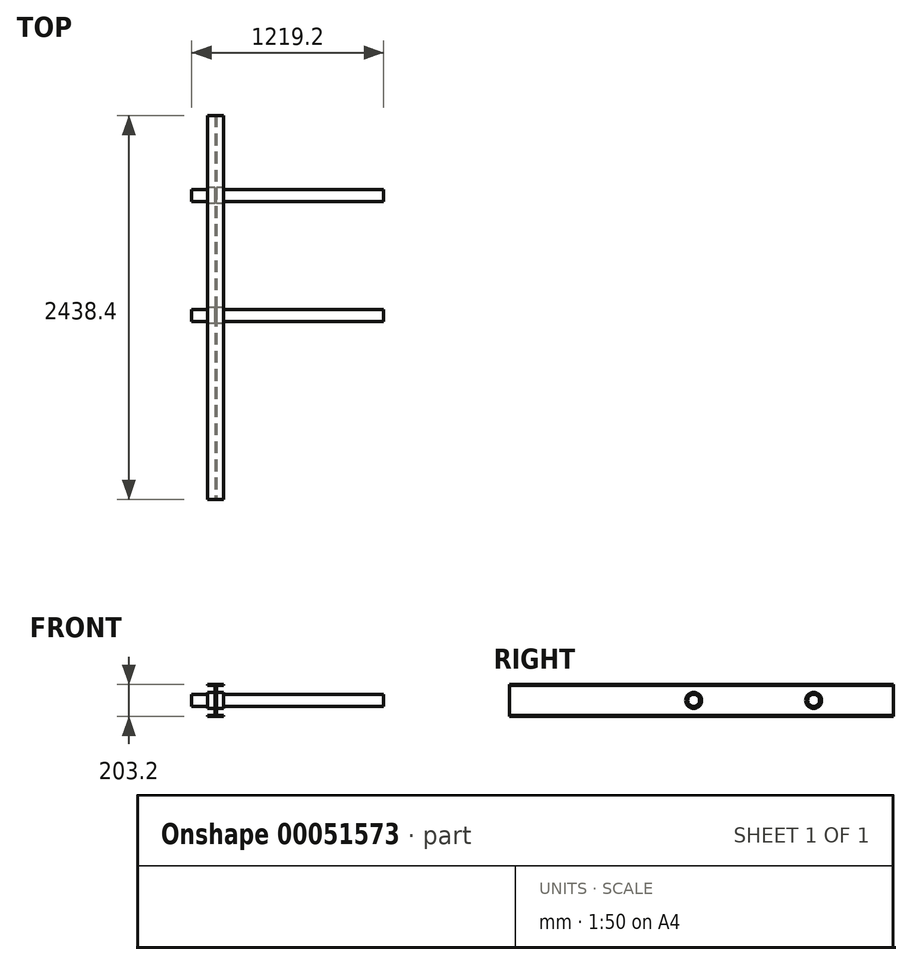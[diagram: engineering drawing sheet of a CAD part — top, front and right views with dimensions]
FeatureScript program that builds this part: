
annotation { "Feature Type Name" : "Feature", "Feature Type Description" : "" }
export const myFeature = defineFeature(function(context is Context, id is Id, definition is map)
    precondition{}
    {
        {
            var Q0;
            Q0=qCreatedBy(makeId("Front.planeOp"),FACE);
            var sketch = newSketch(context, id + "F0", { "sketchPlane" : qUnion([Q0])});
            skLineSegment(sketch, "E0.rect.bottom", {"start": v(50.8, -101.6) * mm, "end": v(-50.8, -101.6) * mm});
            skLineSegment(sketch, "E0.rect.top", {"start": v(50.8, 101.6) * mm, "end": v(-50.8, 101.6) * mm});
            skLineSegment(sketch, "E0.rect.left", {"start": v(50.8, -101.6) * mm, "end": v(50.8, 101.6) * mm});
            skLineSegment(sketch, "E0.rect.right", {"start": v(-50.8, -101.6) * mm, "end": v(-50.8, 101.6) * mm});
            skPoint(sketch, "E0.rect.middle", {"position": v(0, 0) * mm});
            skLineSegment(sketch, "E1.bottom", {"start": v(-50.8, 95.25) * mm, "end": v(-4.76, 95.25) * mm});
            skLineSegment(sketch, "E1.top", {"start": v(-50.8, -95.25) * mm, "end": v(-4.76, -95.25) * mm});
            skLineSegment(sketch, "E1.left", {"start": v(-50.8, 95.25) * mm, "end": v(-50.8, -95.25) * mm});
            skLineSegment(sketch, "E1.right", {"start": v(-4.76, 95.25) * mm, "end": v(-4.76, -95.25) * mm});
            skLineSegment(sketch, "E2.bottom", {"start": v(50.8, 95.25) * mm, "end": v(4.76, 95.25) * mm});
            skLineSegment(sketch, "E2.top", {"start": v(50.8, -95.25) * mm, "end": v(4.76, -95.25) * mm});
            skLineSegment(sketch, "E2.left", {"start": v(50.8, 95.25) * mm, "end": v(50.8, -95.25) * mm});
            skLineSegment(sketch, "E2.right", {"start": v(4.76, 95.25) * mm, "end": v(4.76, -95.25) * mm});
            skSolve(sketch);
        }
        {
            var Q0;
            Q0=makeQuery(id+"F0.imprint","IMPRINT",FACE,{"disambiguationData":[TD([[makeQuery(id+"F0.imprint","IMPRINT",EDGE,{"derivedFrom":sQuery(id+"F0.wireOp",EDGE,"E0.rect.bottom")}),-1.0]])]});
            extrude(context, id + "F1", {"entities" : qUnion([Q0]), "oppositeDirection" : true, "depth" : 2438.4 * mm});
        }
        {
            var Q0;
            Q0=makeQuery(id+"F1.opExtrude","SWEPT_FACE",FACE,{"disambiguationData":[OSD([sQuery(id+"F0.wireOp",EDGE,"E2.right")])]});
            var sketch = newSketch(context, id + "F2", { "sketchPlane" : qUnion([Q0])});
            skCircle(sketch, "E3", {"center": v(1168.4, 0) * mm, "radius": 50.8 * mm});
            skCircle(sketch, "E4", {"center": v(1930.4, 0) * mm, "radius": 50.8 * mm});
            skSolve(sketch);
        }
        {
            var Q0;
            Q0=makeQuery(id+"F2.imprint","IMPRINT",FACE,{"disambiguationData":[TD([[makeQuery(id+"F2.imprint","IMPRINT",EDGE,{"derivedFrom":sQuery(id+"F2.wireOp",EDGE,"E3")}),1.0]])]});
            var Q1;
            Q1=makeQuery(id+"F2.imprint","IMPRINT",FACE,{"disambiguationData":[TD([[makeQuery(id+"F2.imprint","IMPRINT",EDGE,{"derivedFrom":sQuery(id+"F2.wireOp",EDGE,"E4")}),1.0]])]});
            extrude(context, id + "F3", {"entities" : qUnion([Q0, Q1]), "operationType" : NewBodyOperationType.REMOVE, "endBound" : BoundingType.THROUGH_ALL, "oppositeDirection" : true, "depth" : 25.4 * mm});
        }
        {
            var Q0;
            Q0=makeQuery(id+"F1.opExtrude","SWEPT_FACE",FACE,{"disambiguationData":[OSD([sQuery(id+"F0.wireOp",EDGE,"E2.right")])]});
            var sketch = newSketch(context, id + "F4", { "sketchPlane" : qUnion([Q0])});
            skCircle(sketch, "E5", {"center": v(1168.4, 0) * mm, "radius": 38.1 * mm});
            skCircle(sketch, "E6", {"center": v(1930.4, 0) * mm, "radius": 38.1 * mm});
            skSolve(sketch);
        }
        {
            var Q0;
            Q0=makeQuery(id+"F4.imprint","IMPRINT",FACE,{"disambiguationData":[TD([[makeQuery(id+"F4.imprint","IMPRINT",EDGE,{"derivedFrom":sQuery(id+"F4.wireOp",EDGE,"E5")}),-1.0]])]});
            var Q1;
            Q1=makeQuery(id+"F4.imprint","IMPRINT",FACE,{"disambiguationData":[TD([[makeQuery(id+"F4.imprint","IMPRINT",EDGE,{"derivedFrom":sQuery(id+"F4.wireOp",EDGE,"E6")}),-1.0]])]});
            var Q2;
            {var subQ0=sQuery(id+"F0.wireOp",EDGE,"E0.rect.left");Q2=makeQuery(id+"F1.opExtrude","SWEPT_FACE",FACE,{"disambiguationData":[OSD([subQ0]),TDD([makeQuery(id+"F0.imprint","IMPRINT",EDGE,{"disambiguationData":[TD([[makeQuery(id+"F0.imprint","INTERSECT",VERTEX,{"derivedFrom":[sQuery(id+"F0.wireOp",EDGE,"E0.rect.top"),subQ0]}),1.0]])],"derivedFrom":subQ0})])]});}
            var Q3;
            {var subQ0=sQuery(id+"F0.wireOp",EDGE,"E0.rect.right");Q3=makeQuery(id+"F1.opExtrude","SWEPT_FACE",FACE,{"disambiguationData":[OSD([subQ0]),TDD([makeQuery(id+"F0.imprint","IMPRINT",EDGE,{"disambiguationData":[TD([[makeQuery(id+"F0.imprint","INTERSECT",VERTEX,{"derivedFrom":[sQuery(id+"F0.wireOp",EDGE,"E0.rect.top"),subQ0]}),1.0]])],"derivedFrom":subQ0})])]});}
            extrude(context, id + "F5", {"entities" : qUnion([Q0, Q1]), "operationType" : NewBodyOperationType.ADD, "endBound" : BoundingType.UP_TO_SURFACE, "endBoundEntityFace" : qUnion([Q2]), "depth" : 25.4 * mm, "hasSecondDirection" : true, "secondDirectionBound" : SecondDirectionBoundingType.UP_TO_SURFACE, "secondDirectionOppositeDirection" : true, "secondDirectionBoundEntityFace" : qUnion([Q3]), "secondDirectionDepth" : 25.4 * mm});
        }
        {
            var Q0;
            Q0=makeQuery(id+"F5.opExtrude","CAP_FACE",FACE,{"disambiguationData":[OSD([sQuery(id+"F2.wireOp",EDGE,"E3"),sQuery(id+"F4.wireOp",EDGE,"E5")])],"isStart":false});
            var sketch = newSketch(context, id + "F6", { "sketchPlane" : qUnion([Q0])});
            skCircle(sketch, "E7.0", {"center": v(1930.4, 0) * mm, "radius": 38.1 * mm});
            skCircle(sketch, "E8.0", {"center": v(1168.4, 0) * mm, "radius": 38.1 * mm});
            skSolve(sketch);
        }
        {
            var Q0;
            Q0=makeQuery(id+"F6.imprint","IMPRINT",FACE,{"disambiguationData":[TD([[makeQuery(id+"F6.imprint","IMPRINT",EDGE,{"derivedFrom":sQuery(id+"F6.wireOp",EDGE,"E8.0")}),1.0]])]});
            var Q1;
            Q1=makeQuery(id+"F6.imprint","IMPRINT",FACE,{"disambiguationData":[TD([[makeQuery(id+"F6.imprint","IMPRINT",EDGE,{"derivedFrom":sQuery(id+"F6.wireOp",EDGE,"E7.0")}),1.0]])]});
            extrude(context, id + "F7", {"entities" : qUnion([Q0, Q1]), "operationType" : NewBodyOperationType.ADD, "depth" : 1016 * mm, "hasSecondDirection" : true, "secondDirectionOppositeDirection" : true, "secondDirectionDepth" : 203.2 * mm});
        }
    });
